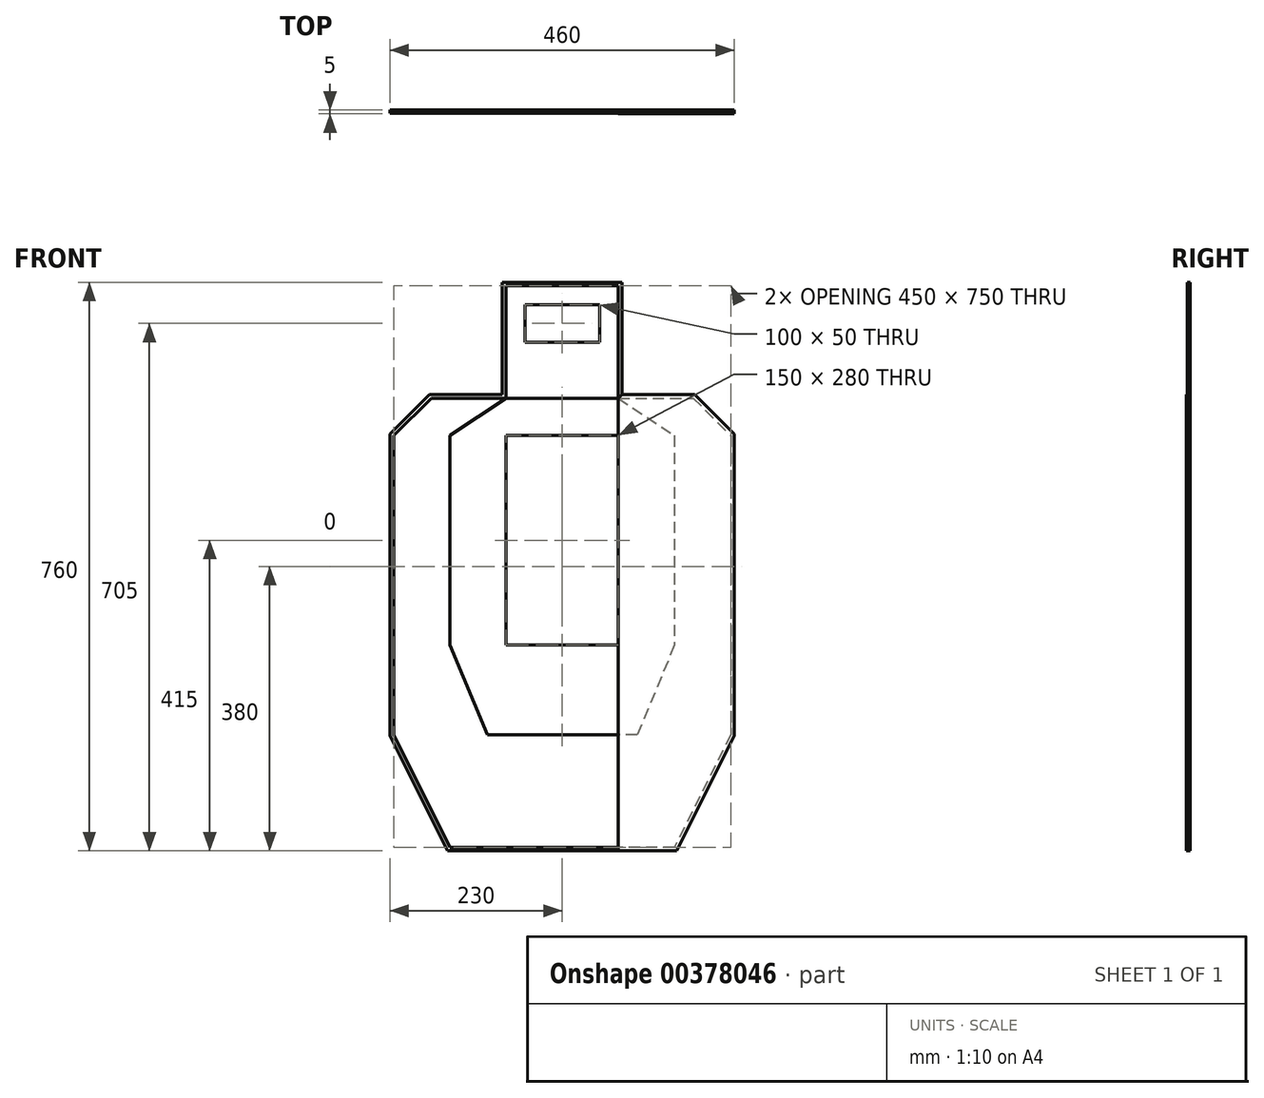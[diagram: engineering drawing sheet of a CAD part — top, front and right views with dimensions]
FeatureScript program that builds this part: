
annotation { "Feature Type Name" : "Feature", "Feature Type Description" : "" }
export const myFeature = defineFeature(function(context is Context, id is Id, definition is map)
    precondition{}
    {
        {
            var Q0;
            Q0=qCreatedBy(makeId("Front.planeOp"),FACE);
            var sketch = newSketch(context, id + "F0", { "sketchPlane" : qUnion([Q0])});
            skLineSegment(sketch, "E0.bottom", {"start": v(0, 100) * mm, "end": v(50, 100) * mm, "construction": true});
            skLineSegment(sketch, "E0.top", {"start": v(0, 125) * mm, "end": v(50, 125) * mm});
            skLineSegment(sketch, "E0.right", {"start": v(50, 100) * mm, "end": v(50, 125) * mm});
            skLineSegment(sketch, "E1.MirrorCS", {"start": v(0, 75) * mm, "end": v(50, 75) * mm});
            skLineSegment(sketch, "E2.MirrorCS", {"start": v(50, 100) * mm, "end": v(50, 75) * mm});
            skLineSegment(sketch, "E3.MirrorCS", {"start": v(0, 0) * mm, "end": v(0, 100) * mm, "construction": true});
            skLineSegment(sketch, "E4.MirrorCS", {"start": v(0, 125) * mm, "end": v(-50, 125) * mm});
            skLineSegment(sketch, "E5.MirrorCS", {"start": v(-50, 100) * mm, "end": v(-50, 125) * mm});
            skLineSegment(sketch, "E6.MirrorCS", {"start": v(-50, 100) * mm, "end": v(-50, 75) * mm});
            skLineSegment(sketch, "E7.MirrorCS", {"start": v(0, 75) * mm, "end": v(-50, 75) * mm});
            skSolve(sketch);
        }
        {
            var Q0;
            Q0=qSketchRegion(id+"F0",true);
            extrude(context, id + "F1", {"entities" : qUnion([Q0]), "oppositeDirection" : true, "depth" : 3 * mm});
        }
        {
            var Q0;
            Q0=qCreatedBy(makeId("Front.planeOp"),FACE);
            var sketch = newSketch(context, id + "F2", { "sketchPlane" : qUnion([Q0])});
            skLineSegment(sketch, "E8", {"start": v(75, 0) * mm, "end": v(75, 150) * mm});
            skLineSegment(sketch, "E9", {"start": v(75, 150) * mm, "end": v(-75, 150) * mm});
            skLineSegment(sketch, "E10", {"start": v(-75, 150) * mm, "end": v(-75, 0) * mm});
            skLineSegment(sketch, "E11", {"start": v(-75, 0) * mm, "end": v(75, 0) * mm});
            skLineSegment(sketch, "E12.0", {"start": v(0, 125) * mm, "end": v(-50, 125) * mm});
            skLineSegment(sketch, "E13.0", {"start": v(0, 125) * mm, "end": v(50, 125) * mm});
            skLineSegment(sketch, "E14.0", {"start": v(50, 100) * mm, "end": v(50, 125) * mm});
            skLineSegment(sketch, "E15.1", {"start": v(50, 100) * mm, "end": v(50, 75) * mm});
            skLineSegment(sketch, "E16.0", {"start": v(0, 75) * mm, "end": v(50, 75) * mm});
            skLineSegment(sketch, "E17.0", {"start": v(0, 75) * mm, "end": v(-50, 75) * mm});
            skLineSegment(sketch, "E18.0", {"start": v(-50, 100) * mm, "end": v(-50, 75) * mm});
            skLineSegment(sketch, "E19.1", {"start": v(-50, 100) * mm, "end": v(-50, 125) * mm});
            skLineSegment(sketch, "E20", {"start": v(0, 125) * mm, "end": v(0, 150) * mm, "construction": true});
            skLineSegment(sketch, "E21", {"start": v(0, 150) * mm, "end": v(0, 137.5) * mm, "construction": true});
            skSolve(sketch);
        }
        {
            var Q0;
            {var subQ0=sQuery(id+"F2.wireOp",EDGE,"E8");Q0=makeQuery(id+"F2.imprint","IMPRINT",FACE,{"disambiguationData":[TD([[makeQuery(id+"F2.imprint","IMPRINT",EDGE,{"derivedFrom":subQ0}),1.0]])]});}
            extrude(context, id + "F3", {"entities" : qUnion([Q0]), "oppositeDirection" : true, "depth" : 3 * mm});
        }
        {
            var Q0;
            Q0=qCreatedBy(makeId("Front.planeOp"),FACE);
            var sketch = newSketch(context, id + "F4", { "sketchPlane" : qUnion([Q0])});
            skLineSegment(sketch, "E22.bottom", {"start": v(75, -50) * mm, "end": v(-75, -50) * mm});
            skLineSegment(sketch, "E22.top", {"start": v(75, -330) * mm, "end": v(-75, -330) * mm});
            skLineSegment(sketch, "E22.left", {"start": v(75, -50) * mm, "end": v(75, -330) * mm});
            skLineSegment(sketch, "E22.right", {"start": v(-75, -50) * mm, "end": v(-75, -330) * mm});
            skLineSegment(sketch, "E23", {"start": v(0, 0) * mm, "end": v(0, -50) * mm, "construction": true});
            skLineSegment(sketch, "E24.0", {"start": v(-75, 0) * mm, "end": v(75, 0) * mm, "construction": true});
            skLineSegment(sketch, "E25", {"start": v(75, 0) * mm, "end": v(75, -50) * mm, "construction": true});
            skSolve(sketch);
        }
        {
            var Q0;
            Q0=makeQuery(id+"F4.imprint","IMPRINT",FACE,{"disambiguationData":[TD([[makeQuery(id+"F4.imprint","IMPRINT",EDGE,{"derivedFrom":sQuery(id+"F4.wireOp",EDGE,"E22.bottom")}),1.0]])]});
            extrude(context, id + "F5", {"entities" : qUnion([Q0]), "oppositeDirection" : true, "depth" : 3 * mm});
        }
        {
            var Q0;
            Q0=qCreatedBy(makeId("Front.planeOp"),FACE);
            var sketch = newSketch(context, id + "F6", { "sketchPlane" : qUnion([Q0])});
            skLineSegment(sketch, "E26.0", {"start": v(-75, 0) * mm, "end": v(75, 0) * mm});
            skLineSegment(sketch, "E27.1", {"start": v(75, -50) * mm, "end": v(75, -330) * mm});
            skLineSegment(sketch, "E28.2", {"start": v(75, -50) * mm, "end": v(-75, -50) * mm});
            skLineSegment(sketch, "E29.3", {"start": v(-75, -50) * mm, "end": v(-75, -330) * mm});
            skLineSegment(sketch, "E30.0", {"start": v(75, -330) * mm, "end": v(-75, -330) * mm});
            skLineSegment(sketch, "E31", {"start": v(75, 0) * mm, "end": v(150, -50) * mm});
            skLineSegment(sketch, "E32", {"start": v(150, -50) * mm, "end": v(150, -330) * mm});
            skLineSegment(sketch, "E33", {"start": v(150, -330) * mm, "end": v(100, -450) * mm});
            skLineSegment(sketch, "E34", {"start": v(100, -450) * mm, "end": v(-100, -450) * mm});
            skLineSegment(sketch, "E35", {"start": v(-100, -450) * mm, "end": v(-150, -330) * mm});
            skLineSegment(sketch, "E36", {"start": v(-150, -330) * mm, "end": v(-150, -50) * mm});
            skLineSegment(sketch, "E37", {"start": v(-150, -50) * mm, "end": v(-75, 0) * mm});
            skLineSegment(sketch, "E38", {"start": v(0, -450) * mm, "end": v(0, -50) * mm, "construction": true});
            skLineSegment(sketch, "E39", {"start": v(150, -50) * mm, "end": v(75, -50) * mm, "construction": true});
            skLineSegment(sketch, "E40", {"start": v(-55.04, -50) * mm, "end": v(-150, -50) * mm, "construction": true});
            skLineSegment(sketch, "E41", {"start": v(150, -330) * mm, "end": v(150, -450) * mm, "construction": true});
            skLineSegment(sketch, "E42", {"start": v(100, -450) * mm, "end": v(150, -450) * mm, "construction": true});
            skLineSegment(sketch, "E43", {"start": v(150, -330) * mm, "end": v(-150, -330) * mm, "construction": true});
            skLineSegment(sketch, "E44", {"start": v(-150, -330) * mm, "end": v(-150, -450) * mm, "construction": true});
            skLineSegment(sketch, "E45", {"start": v(-150, -450) * mm, "end": v(-100, -450) * mm, "construction": true});
            skSolve(sketch);
        }
        {
            var Q0;
            Q0=makeQuery(id+"F6.imprint","IMPRINT",FACE,{"disambiguationData":[TD([[makeQuery(id+"F6.imprint","IMPRINT",EDGE,{"derivedFrom":sQuery(id+"F6.wireOp",EDGE,"E26.0")}),-1.0]])]});
            extrude(context, id + "F7", {"entities" : qUnion([Q0]), "oppositeDirection" : true, "depth" : 3 * mm});
        }
        {
            var Q0;
            Q0=makeQuery(id+"F7.opExtrude","CAP_FACE",FACE,{"disambiguationData":[OSD([sQuery(id+"F6.wireOp",EDGE,"E26.0"),sQuery(id+"F6.wireOp",EDGE,"E27.1"),sQuery(id+"F6.wireOp",EDGE,"E28.2"),sQuery(id+"F6.wireOp",EDGE,"E29.3"),sQuery(id+"F6.wireOp",EDGE,"E30.0"),sQuery(id+"F6.wireOp",EDGE,"E31"),sQuery(id+"F6.wireOp",EDGE,"E32"),sQuery(id+"F6.wireOp",EDGE,"E33"),sQuery(id+"F6.wireOp",EDGE,"E34"),sQuery(id+"F6.wireOp",EDGE,"E35"),sQuery(id+"F6.wireOp",EDGE,"E36"),sQuery(id+"F6.wireOp",EDGE,"E37")])],"isStart":true});
            var sketch = newSketch(context, id + "F8", { "sketchPlane" : qUnion([Q0])});
            skLineSegment(sketch, "E46.0", {"start": v(75, 0) * mm, "end": v(150, -50) * mm});
            skLineSegment(sketch, "E47.0", {"start": v(150, -50) * mm, "end": v(150, -330) * mm});
            skLineSegment(sketch, "E48.0", {"start": v(150, -330) * mm, "end": v(100, -450) * mm});
            skLineSegment(sketch, "E49.1", {"start": v(100, -450) * mm, "end": v(-100, -450) * mm});
            skLineSegment(sketch, "E50.0", {"start": v(-150, -330) * mm, "end": v(-150, -50) * mm});
            skLineSegment(sketch, "E51.0", {"start": v(-100, -450) * mm, "end": v(-150, -330) * mm});
            skLineSegment(sketch, "E52.0", {"start": v(-150, -50) * mm, "end": v(-75, 0) * mm});
            skLineSegment(sketch, "E53", {"start": v(75, 0) * mm, "end": v(175, 0) * mm});
            skLineSegment(sketch, "E54", {"start": v(175, 0) * mm, "end": v(225, -50) * mm});
            skLineSegment(sketch, "E55", {"start": v(225, -50) * mm, "end": v(225, -450) * mm});
            skLineSegment(sketch, "E56", {"start": v(225, -450) * mm, "end": v(150, -600) * mm});
            skLineSegment(sketch, "E57", {"start": v(150, -600) * mm, "end": v(-150, -600) * mm});
            skLineSegment(sketch, "E58", {"start": v(-150, -600) * mm, "end": v(-225, -450) * mm});
            skLineSegment(sketch, "E59", {"start": v(-225, -450) * mm, "end": v(-225, -50) * mm});
            skLineSegment(sketch, "E60", {"start": v(-225, -50) * mm, "end": v(-175, 0) * mm});
            skLineSegment(sketch, "E61", {"start": v(-175, 0) * mm, "end": v(-75, 0) * mm});
            skLineSegment(sketch, "E62", {"start": v(225, -50) * mm, "end": v(225, 0) * mm, "construction": true});
            skLineSegment(sketch, "E63", {"start": v(225, 0) * mm, "end": v(175, 0) * mm, "construction": true});
            skLineSegment(sketch, "E64", {"start": v(225, -450) * mm, "end": v(225, -600) * mm, "construction": true});
            skLineSegment(sketch, "E65", {"start": v(225, -600) * mm, "end": v(150, -600) * mm, "construction": true});
            skLineSegment(sketch, "E66", {"start": v(-225, -450) * mm, "end": v(-225, -600) * mm, "construction": true});
            skLineSegment(sketch, "E67", {"start": v(-225, -600) * mm, "end": v(-150, -600) * mm, "construction": true});
            skLineSegment(sketch, "E68", {"start": v(-175, 0) * mm, "end": v(-225, 0) * mm, "construction": true});
            skLineSegment(sketch, "E69", {"start": v(-225, 0) * mm, "end": v(-225, -50) * mm, "construction": true});
            skSolve(sketch);
        }
        {
            var Q0;
            Q0=qSketchRegion(id+"F8",true);
            extrude(context, id + "F9", {"entities" : qUnion([Q0]), "oppositeDirection" : true, "depth" : 3 * mm});
        }
        {
            var Q0;
            Q0=makeQuery(id+"F9.opExtrude","CAP_FACE",FACE,{"disambiguationData":[OSD([sQuery(id+"F8.wireOp",EDGE,"E46.0"),sQuery(id+"F8.wireOp",EDGE,"E47.0"),sQuery(id+"F8.wireOp",EDGE,"E48.0"),sQuery(id+"F8.wireOp",EDGE,"E49.1"),sQuery(id+"F8.wireOp",EDGE,"E50.0"),sQuery(id+"F8.wireOp",EDGE,"E51.0"),sQuery(id+"F8.wireOp",EDGE,"E52.0"),sQuery(id+"F8.wireOp",EDGE,"E53"),sQuery(id+"F8.wireOp",EDGE,"E54"),sQuery(id+"F8.wireOp",EDGE,"E55"),sQuery(id+"F8.wireOp",EDGE,"E56"),sQuery(id+"F8.wireOp",EDGE,"E57"),sQuery(id+"F8.wireOp",EDGE,"E58"),sQuery(id+"F8.wireOp",EDGE,"E59"),sQuery(id+"F8.wireOp",EDGE,"E60"),sQuery(id+"F8.wireOp",EDGE,"E61")])],"isStart":true});
            var sketch = newSketch(context, id + "F10", { "sketchPlane" : qUnion([Q0])});
            skLineSegment(sketch, "E70.0", {"start": v(75, 150) * mm, "end": v(-75, 150) * mm});
            skLineSegment(sketch, "E71.0", {"start": v(75, 0) * mm, "end": v(75, 150) * mm});
            skLineSegment(sketch, "E72.1", {"start": v(75, 0) * mm, "end": v(175, 0) * mm});
            skLineSegment(sketch, "E73.0", {"start": v(175, 0) * mm, "end": v(225, -50) * mm});
            skLineSegment(sketch, "E74.1", {"start": v(225, -50) * mm, "end": v(225, -450) * mm});
            skLineSegment(sketch, "E75.0", {"start": v(225, -450) * mm, "end": v(150, -600) * mm});
            skLineSegment(sketch, "E76.1", {"start": v(150, -600) * mm, "end": v(-150, -600) * mm});
            skLineSegment(sketch, "E77.2", {"start": v(-150, -600) * mm, "end": v(-225, -450) * mm});
            skLineSegment(sketch, "E78.3", {"start": v(-225, -450) * mm, "end": v(-225, -50) * mm});
            skLineSegment(sketch, "E79.4", {"start": v(-225, -50) * mm, "end": v(-175, 0) * mm});
            skLineSegment(sketch, "E80.5", {"start": v(-175, 0) * mm, "end": v(-75, 0) * mm});
            skLineSegment(sketch, "E81.0", {"start": v(-75, 150) * mm, "end": v(-75, 0) * mm});
            skLineSegment(sketch, "E82.0", {"start": v(177.07, 5) * mm, "end": v(230, -47.93) * mm});
            skLineSegment(sketch, "E82.1", {"start": v(-230, -451.18) * mm, "end": v(-230, -47.93) * mm});
            skLineSegment(sketch, "E82.2", {"start": v(-153.1, -605) * mm, "end": v(-230, -451.18) * mm});
            skLineSegment(sketch, "E82.3", {"start": v(153.1, -605) * mm, "end": v(-153.1, -605) * mm});
            skLineSegment(sketch, "E82.4", {"start": v(230, -451.18) * mm, "end": v(153.1, -605) * mm});
            skLineSegment(sketch, "E82.5", {"start": v(-230, -47.93) * mm, "end": v(-177.07, 5) * mm});
            skLineSegment(sketch, "E82.6", {"start": v(230, -47.93) * mm, "end": v(230, -451.18) * mm});
            skLineSegment(sketch, "E82.7", {"start": v(-177.07, 5) * mm, "end": v(-80, 5) * mm});
            skLineSegment(sketch, "E82.8", {"start": v(-80, 155) * mm, "end": v(-80, 5) * mm});
            skLineSegment(sketch, "E82.9", {"start": v(80, 155) * mm, "end": v(-80, 155) * mm});
            skLineSegment(sketch, "E82.10", {"start": v(80, 5) * mm, "end": v(80, 155) * mm});
            skLineSegment(sketch, "E82.11", {"start": v(80, 5) * mm, "end": v(177.07, 5) * mm});
            skSolve(sketch);
        }
        {
            var Q0;
            Q0=makeQuery(id+"F10.imprint","IMPRINT",FACE,{"disambiguationData":[TD([[makeQuery(id+"F10.imprint","IMPRINT",EDGE,{"derivedFrom":sQuery(id+"F10.wireOp",EDGE,"E70.0")}),-1.0]])]});
            extrude(context, id + "F11", {"entities" : qUnion([Q0]), "oppositeDirection" : true, "depth" : 3 * mm});
        }
        {
            var Q0;
            Q0=makeQuery(id+"F9.opExtrude","CAP_FACE",FACE,{"disambiguationData":[OSD([sQuery(id+"F8.wireOp",EDGE,"E46.0"),sQuery(id+"F8.wireOp",EDGE,"E47.0"),sQuery(id+"F8.wireOp",EDGE,"E48.0"),sQuery(id+"F8.wireOp",EDGE,"E49.1"),sQuery(id+"F8.wireOp",EDGE,"E50.0"),sQuery(id+"F8.wireOp",EDGE,"E51.0"),sQuery(id+"F8.wireOp",EDGE,"E52.0"),sQuery(id+"F8.wireOp",EDGE,"E53"),sQuery(id+"F8.wireOp",EDGE,"E54"),sQuery(id+"F8.wireOp",EDGE,"E55"),sQuery(id+"F8.wireOp",EDGE,"E56"),sQuery(id+"F8.wireOp",EDGE,"E57"),sQuery(id+"F8.wireOp",EDGE,"E58"),sQuery(id+"F8.wireOp",EDGE,"E59"),sQuery(id+"F8.wireOp",EDGE,"E60"),sQuery(id+"F8.wireOp",EDGE,"E61")])],"isStart":false});
            var sketch = newSketch(context, id + "F12", { "sketchPlane" : qUnion([Q0])});
            skLineSegment(sketch, "E83.0", {"start": v(75, 150) * mm, "end": v(75, 0) * mm});
            skLineSegment(sketch, "E84.0", {"start": v(175, 0) * mm, "end": v(75, 0) * mm});
            skLineSegment(sketch, "E85.0", {"start": v(-75, 150) * mm, "end": v(75, 150) * mm});
            skLineSegment(sketch, "E86.0", {"start": v(225, -50) * mm, "end": v(175, 0) * mm});
            skLineSegment(sketch, "E87.0", {"start": v(-225, -50) * mm, "end": v(-225, -450) * mm});
            skLineSegment(sketch, "E87.1", {"start": v(225, -450) * mm, "end": v(225, -50) * mm});
            skLineSegment(sketch, "E87.2", {"start": v(150, -600) * mm, "end": v(225, -450) * mm});
            skLineSegment(sketch, "E87.3", {"start": v(-225, -450) * mm, "end": v(-150, -600) * mm});
            skLineSegment(sketch, "E87.4", {"start": v(-150, -600) * mm, "end": v(150, -600) * mm});
            skLineSegment(sketch, "E88.0", {"start": v(-175, 0) * mm, "end": v(-225, -50) * mm});
            skLineSegment(sketch, "E89.0", {"start": v(-75, 0) * mm, "end": v(-175, 0) * mm});
            skLineSegment(sketch, "E90.0", {"start": v(-75, 0) * mm, "end": v(-75, 150) * mm});
            skSolve(sketch);
        }
        {
            var Q0;
            Q0=qSketchRegion(id+"F12",true);
            extrude(context, id + "F13", {"entities" : qUnion([Q0]), "depth" : 1 * mm});
        }
        {
            var Q0;
            Q0=makeQuery(id+"F13.opExtrude","CAP_FACE",FACE,{"disambiguationData":[OSD([sQuery(id+"F12.wireOp",EDGE,"E83.0"),sQuery(id+"F12.wireOp",EDGE,"E84.0"),sQuery(id+"F12.wireOp",EDGE,"E85.0"),sQuery(id+"F12.wireOp",EDGE,"E86.0"),sQuery(id+"F12.wireOp",EDGE,"E87.0"),sQuery(id+"F12.wireOp",EDGE,"E87.1"),sQuery(id+"F12.wireOp",EDGE,"E87.2"),sQuery(id+"F12.wireOp",EDGE,"E87.3"),sQuery(id+"F12.wireOp",EDGE,"E87.4"),sQuery(id+"F12.wireOp",EDGE,"E88.0"),sQuery(id+"F12.wireOp",EDGE,"E89.0"),sQuery(id+"F12.wireOp",EDGE,"E90.0")])],"isStart":false});
            var sketch = newSketch(context, id + "F14", { "sketchPlane" : qUnion([Q0])});
            skLineSegment(sketch, "E91.0", {"start": v(-80, 155) * mm, "end": v(80, 155) * mm});
            skLineSegment(sketch, "E92.0", {"start": v(80, 155) * mm, "end": v(80, 5) * mm});
            skLineSegment(sketch, "E93.0", {"start": v(-80, 5) * mm, "end": v(-80, 155) * mm});
            skLineSegment(sketch, "E94.0", {"start": v(177.07, 5) * mm, "end": v(80, 5) * mm});
            skLineSegment(sketch, "E95.0", {"start": v(-80, 5) * mm, "end": v(-177.07, 5) * mm});
            skLineSegment(sketch, "E96.0", {"start": v(230, -47.93) * mm, "end": v(177.07, 5) * mm});
            skLineSegment(sketch, "E97.0", {"start": v(-177.07, 5) * mm, "end": v(-230, -47.93) * mm});
            skLineSegment(sketch, "E98.1", {"start": v(-230, -47.93) * mm, "end": v(-230, -451.18) * mm});
            skLineSegment(sketch, "E99.0", {"start": v(-230, -451.18) * mm, "end": v(-153.1, -605) * mm});
            skLineSegment(sketch, "E100.0", {"start": v(-153.1, -605) * mm, "end": v(153.1, -605) * mm});
            skLineSegment(sketch, "E101.0", {"start": v(153.1, -605) * mm, "end": v(230, -451.18) * mm});
            skLineSegment(sketch, "E102.0", {"start": v(230, -451.18) * mm, "end": v(230, -47.93) * mm});
            skLineSegment(sketch, "E103.0", {"start": v(-75, 150) * mm, "end": v(75, 150) * mm});
            skLineSegment(sketch, "E104.0", {"start": v(-75, 0) * mm, "end": v(-75, 150) * mm});
            skLineSegment(sketch, "E105.0", {"start": v(75, 150) * mm, "end": v(75, 0) * mm});
            skLineSegment(sketch, "E106.0", {"start": v(175, 0) * mm, "end": v(75, 0) * mm});
            skLineSegment(sketch, "E107.0", {"start": v(225, -50) * mm, "end": v(175, 0) * mm});
            skLineSegment(sketch, "E108.0", {"start": v(150, -600) * mm, "end": v(225, -450) * mm});
            skLineSegment(sketch, "E109.0", {"start": v(225, -450) * mm, "end": v(225, -50) * mm});
            skLineSegment(sketch, "E110.0", {"start": v(-150, -600) * mm, "end": v(150, -600) * mm});
            skLineSegment(sketch, "E111.0", {"start": v(-225, -450) * mm, "end": v(-150, -600) * mm});
            skLineSegment(sketch, "E112.0", {"start": v(-225, -50) * mm, "end": v(-225, -450) * mm});
            skLineSegment(sketch, "E113.0", {"start": v(-175, 0) * mm, "end": v(-225, -50) * mm});
            skLineSegment(sketch, "E114.0", {"start": v(-75, 0) * mm, "end": v(-175, 0) * mm});
            skSolve(sketch);
        }
        {
            var Q0;
            Q0=makeQuery(id+"F14.imprint","IMPRINT",FACE,{"disambiguationData":[TD([[makeQuery(id+"F14.imprint","IMPRINT",EDGE,{"derivedFrom":sQuery(id+"F14.wireOp",EDGE,"E91.0")}),-1.0]])]});
            extrude(context, id + "F15", {"entities" : qUnion([Q0]), "oppositeDirection" : true, "depth" : 1 * mm});
        }
        {
            var Q0;
            Q0=makeQuery(id+"F9.opExtrude","CAP_FACE",FACE,{"disambiguationData":[OSD([sQuery(id+"F8.wireOp",EDGE,"E46.0"),sQuery(id+"F8.wireOp",EDGE,"E47.0"),sQuery(id+"F8.wireOp",EDGE,"E48.0"),sQuery(id+"F8.wireOp",EDGE,"E49.1"),sQuery(id+"F8.wireOp",EDGE,"E50.0"),sQuery(id+"F8.wireOp",EDGE,"E51.0"),sQuery(id+"F8.wireOp",EDGE,"E52.0"),sQuery(id+"F8.wireOp",EDGE,"E53"),sQuery(id+"F8.wireOp",EDGE,"E54"),sQuery(id+"F8.wireOp",EDGE,"E55"),sQuery(id+"F8.wireOp",EDGE,"E56"),sQuery(id+"F8.wireOp",EDGE,"E57"),sQuery(id+"F8.wireOp",EDGE,"E58"),sQuery(id+"F8.wireOp",EDGE,"E59"),sQuery(id+"F8.wireOp",EDGE,"E60"),sQuery(id+"F8.wireOp",EDGE,"E61")])],"isStart":true});
            var sketch = newSketch(context, id + "F16", { "sketchPlane" : qUnion([Q0])});
            skLineSegment(sketch, "E115.0", {"start": v(80, 5) * mm, "end": v(177.07, 5) * mm});
            skLineSegment(sketch, "E116.0", {"start": v(177.07, 5) * mm, "end": v(230, -47.93) * mm});
            skLineSegment(sketch, "E117.0", {"start": v(153.1, -605) * mm, "end": v(75, -605) * mm});
            skLineSegment(sketch, "E118.0", {"start": v(230, -451.18) * mm, "end": v(153.1, -605) * mm});
            skLineSegment(sketch, "E119.0", {"start": v(230, -47.93) * mm, "end": v(230, -451.18) * mm});
            skLineSegment(sketch, "E120", {"start": v(80, 5) * mm, "end": v(75, 0) * mm});
            skLineSegment(sketch, "E121", {"start": v(75, 0) * mm, "end": v(75, -605) * mm});
            skSolve(sketch);
        }
        {
            var Q0;
            Q0=qSketchRegion(id+"F16",true);
            extrude(context, id + "F17", {"entities" : qUnion([Q0]), "depth" : 1 * mm});
        }
    });
